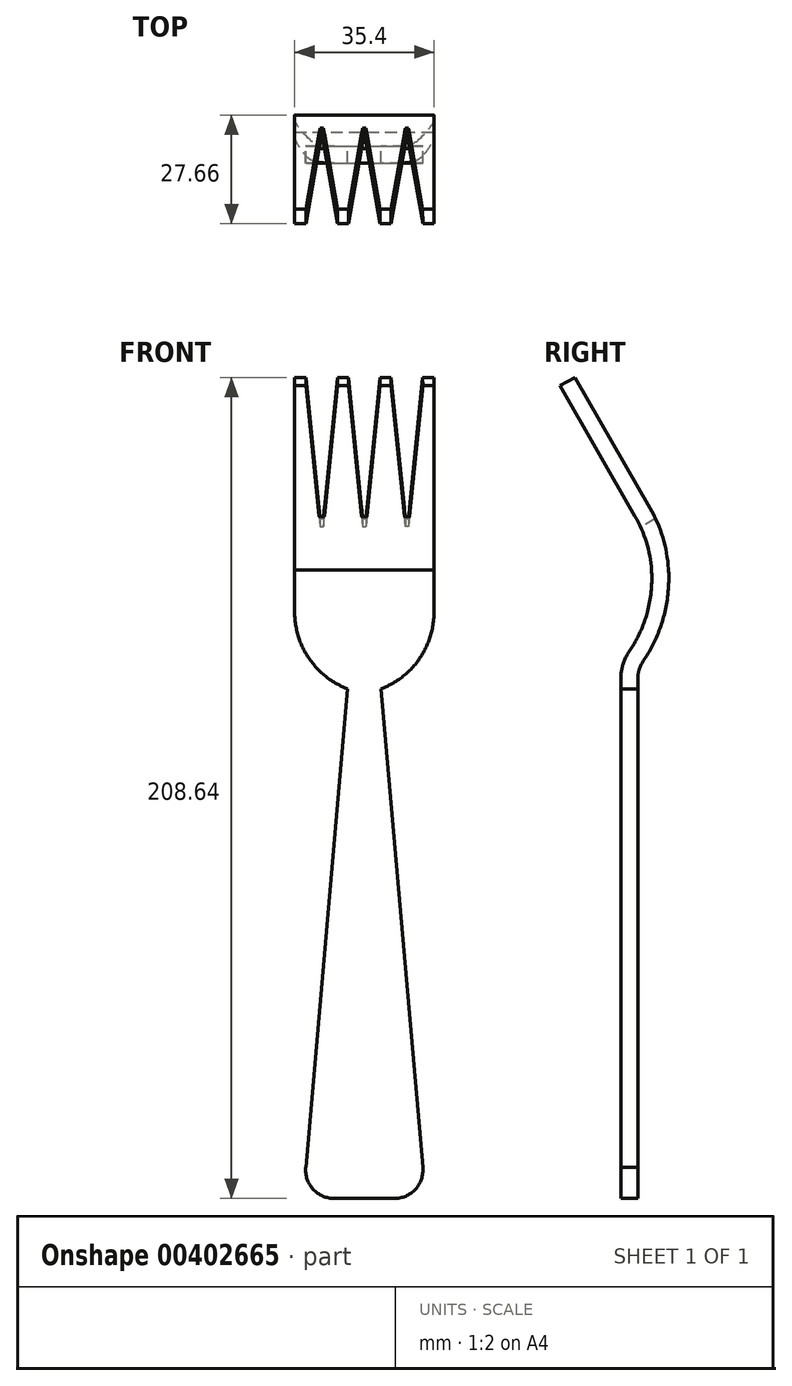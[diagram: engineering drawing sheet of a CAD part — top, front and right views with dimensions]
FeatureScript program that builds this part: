
annotation { "Feature Type Name" : "Feature", "Feature Type Description" : "" }
export const myFeature = defineFeature(function(context is Context, id is Id, definition is map)
    precondition{}
    {
        {
            var Q0;
            Q0=qCreatedBy(makeId("Front.planeOp"),FACE);
            var sketch = newSketch(context, id + "F0", { "sketchPlane" : qUnion([Q0])});
            skLineSegment(sketch, "E0", {"start": v(-7.62, -76.57) * mm, "end": v(7.62, -76.57) * mm});
            skArc(sketch, "E1", {"start": v(-7.62, -76.57) * mm, "mid": v(-12.97, -74.22) * mm, "end": v(-14.85, -68.68) * mm});
            skArc(sketch, "E2", {"start": v(7.62, -76.57) * mm, "mid": v(12.98, -74.22) * mm, "end": v(14.88, -68.68) * mm});
            skLineSegment(sketch, "E3", {"start": v(-14.85, -68.68) * mm, "end": v(14.88, -68.68) * mm});
            skLineSegment(sketch, "E4", {"start": v(-14.85, -68.68) * mm, "end": v(-7.18, 19.15) * mm});
            skLineSegment(sketch, "E5", {"start": v(-7.18, 19.15) * mm, "end": v(-4.23, 52.93) * mm});
            skLineSegment(sketch, "E6.MirrorCS", {"start": v(7.18, 19.15) * mm, "end": v(4.23, 52.93) * mm});
            skLineSegment(sketch, "E7.MirrorCS", {"start": v(14.85, -68.68) * mm, "end": v(7.18, 19.15) * mm});
            skLineSegment(sketch, "E8", {"start": v(-4.23, 52.93) * mm, "end": v(4.23, 52.93) * mm});
            skSolve(sketch);
        }
        {
            var Q0;
            Q0 = qSketchRegion(id + "F0", true);
            extrude(context, id + "F1", {"entities" : qUnion([Q0]), "depth" : 4.32 * mm});
        }
        {
            var Q0;
            Q0=qCreatedBy(makeId("Right.planeOp"),FACE);
            var sketch = newSketch(context, id + "F2", { "sketchPlane" : qUnion([Q0])});
            skPoint(sketch, "E9.0", {"position": v(-4.32, 52.93) * mm});
            skLineSegment(sketch, "E10", {"start": v(-4.32, 52.93) * mm, "end": v(-4.32, 55.36) * mm});
            skArc(sketch, "E11", {"start": v(-2.1, 62.52) * mm, "mid": v(2.37, 72.1) * mm, "end": v(3.54, 82.62) * mm});
            skPoint(sketch, "E12.visualSharp", {"position": v(-4.32, 59.64) * mm});
            skArc(sketch, "E12.filletArc", {"start": v(-2.1, 62.52) * mm, "mid": v(-3.75, 59.1) * mm, "end": v(-4.32, 55.36) * mm});
            skSolve(sketch);
        }
        {
            var Q0;
            Q0=makeQuery(id+"F1.opExtrude","SWEPT_FACE",FACE,{"disambiguationData":[OSD([sQuery(id+"F0.wireOp",EDGE,"E8")])]});
            var Q1;
            Q1=sQuery(id+"F2.wireOp",EDGE,"E10");
            var Q2;
            Q2=sQuery(id+"F2.wireOp",EDGE,"E12.filletArc");
            var Q3;
            Q3=sQuery(id+"F2.wireOp",EDGE,"E11");
            sweep(context, id + "F3", {"operationType" : NewBodyOperationType.ADD, "profiles" : qUnion([Q0]), "path" : qUnion([Q1, Q2, Q3])});
        }
        {
            var Q0;
            Q0=makeQuery(id+"F3.opSweep","CAP_FACE",FACE,{"disambiguationData":[OSD([sQuery(id+"F0.wireOp",EDGE,"E8"),sQuery(id+"F2.wireOp",VERTEX,"E11.end")])],"isStart":false});
            var sketch = newSketch(context, id + "F4", { "sketchPlane" : qUnion([Q0])});
            skLineSegment(sketch, "E13.0.0", {"start": v(4.23, 12.14) * mm, "end": v(-4.23, 12.14) * mm});
            skLineSegment(sketch, "E13.0.1", {"start": v(-4.23, 12.14) * mm, "end": v(-4.23, 7.82) * mm});
            skLineSegment(sketch, "E13.0.2", {"start": v(-4.23, 7.82) * mm, "end": v(4.23, 7.82) * mm});
            skLineSegment(sketch, "E13.0.3", {"start": v(4.23, 7.82) * mm, "end": v(4.23, 12.14) * mm});
            skSolve(sketch);
        }
        {
            var Q0;
            Q0 = qSketchRegion(id + "F4", true);
            extrude(context, id + "F5", {"entities" : qUnion([Q0]), "operationType" : NewBodyOperationType.ADD, "depth" : 0.5 * mm});
        }
        {
            var Q0;
            Q0=makeQuery(id+"F5.boolean.opBoolean","MERGE",FACE,{"derivedFrom":[makeQuery(id+"F3.opSweep","SWEPT_FACE",FACE,{"disambiguationData":[OSD([sQuery(id+"F0.wireOp",EDGE,"E6.MirrorCS"),sQuery(id+"F0.wireOp",EDGE,"E8"),sQuery(id+"F2.wireOp",EDGE,"E10")])]}),makeQuery(id+"F5.opExtrude","SWEPT_FACE",FACE,{"disambiguationData":[OSD([sQuery(id+"F4.wireOp",EDGE,"E13.0.3")])]})]});
            var sketch = newSketch(context, id + "F6", { "sketchPlane" : qUnion([Q0])});
            skLineSegment(sketch, "E14.0.0", {"start": v(0, 52.93) * mm, "end": v(0, 55.36) * mm});
            skArc(sketch, "E14.0.1", {"start": v(0, 55.36) * mm, "mid": v(0.37, 57.83) * mm, "end": v(1.46, 60.09) * mm});
            skArc(sketch, "E14.0.2", {"start": v(1.46, 60.09) * mm, "mid": v(6.52, 70.94) * mm, "end": v(7.85, 82.84) * mm});
            skLineSegment(sketch, "E14.0.3", {"start": v(7.85, 82.84) * mm, "end": v(7.82, 83.35) * mm});
            skLineSegment(sketch, "E14.0.4", {"start": v(7.82, 83.35) * mm, "end": v(3.51, 83.12) * mm});
            skLineSegment(sketch, "E14.0.5", {"start": v(3.51, 83.12) * mm, "end": v(3.54, 82.62) * mm});
            skArc(sketch, "E14.0.6", {"start": v(3.54, 82.62) * mm, "mid": v(2.37, 72.1) * mm, "end": v(-2.1, 62.52) * mm});
            skArc(sketch, "E14.0.7", {"start": v(-2.1, 62.52) * mm, "mid": v(-3.75, 59.1) * mm, "end": v(-4.32, 55.36) * mm});
            skLineSegment(sketch, "E14.0.8", {"start": v(-4.32, 55.36) * mm, "end": v(-4.32, 52.93) * mm});
            skLineSegment(sketch, "E14.0.9", {"start": v(-4.32, 52.93) * mm, "end": v(0, 52.93) * mm});
            skSolve(sketch);
        }
        {
            var Q0;
            Q0 = qSketchRegion(id + "F6", true);
            extrude(context, id + "F7", {"entities" : qUnion([Q0]), "operationType" : NewBodyOperationType.ADD, "depth" : 13.46 * mm});
        }
        {
            var Q0;
            Q0=makeQuery(id+"F1.opExtrude","SWEPT_BODY",BODY,{"disambiguationData":[OSD([sQuery(id+"F0.wireOp",EDGE,"E0"),sQuery(id+"F0.wireOp",EDGE,"E1"),sQuery(id+"F0.wireOp",EDGE,"E2"),sQuery(id+"F0.wireOp",EDGE,"E3"),sQuery(id+"F0.wireOp",EDGE,"E4"),sQuery(id+"F0.wireOp",EDGE,"E5"),sQuery(id+"F0.wireOp",EDGE,"E6.MirrorCS"),sQuery(id+"F0.wireOp",EDGE,"E7.MirrorCS"),sQuery(id+"F0.wireOp",EDGE,"E8")])]});
            var Q1;
            Q1=qCreatedBy(makeId("Right.planeOp"),FACE);
            mirror(context, id + "F8", {"operationType" : NewBodyOperationType.ADD, "entities" : qUnion([Q0]), "mirrorPlane" : qUnion([Q1])});
        }
        {
            var Q0;
            Q0=makeQuery(id+"F7.opExtrude","CAP_EDGE",EDGE,{"disambiguationData":[OSD([sQuery(id+"F6.wireOp",EDGE,"E14.0.9")])],"isStart":false});
            fillet(context, id + "F9", {"entities" : qUnion([Q0]), "radius" : 20.85 * mm, "tangentPropagation" : true, "allowEdgeOverflow" : false});
        }
        {
            var Q0;
            Q0=makeQuery(id+"F8.opPattern","COPY",EDGE,{"derivedFrom":makeQuery(id+"F7.opExtrude","CAP_EDGE",EDGE,{"disambiguationData":[OSD([sQuery(id+"F6.wireOp",EDGE,"E14.0.9")])],"isStart":false}),"instanceName":"1"});
            fillet(context, id + "F10", {"entities" : qUnion([Q0]), "radius" : 20.85 * mm, "tangentPropagation" : true, "allowEdgeOverflow" : false});
        }
        {
            var Q0;
            Q0=qCreatedBy(makeId("Right.planeOp"),FACE);
            var sketch = newSketch(context, id + "F11", { "sketchPlane" : qUnion([Q0])});
            skPoint(sketch, "E15.0", {"position": v(5.67, 83.24) * mm});
            skArc(sketch, "E16", {"start": v(5.67, 83.24) * mm, "mid": v(4.3, 90.77) * mm, "end": v(1.25, 97.8) * mm});
            skLineSegment(sketch, "E17", {"start": v(1.25, 97.8) * mm, "end": v(-17.87, 131.02) * mm});
            skSolve(sketch);
        }
        {
            var Q0;
            {var subQ0=makeQuery(id+"F7.boolean.opBoolean","MERGE",FACE,{"derivedFrom":[makeQuery(id+"F5.opExtrude","CAP_FACE",FACE,{"disambiguationData":[OSD([sQuery(id+"F4.wireOp",EDGE,"E13.0.0"),sQuery(id+"F4.wireOp",EDGE,"E13.0.1"),sQuery(id+"F4.wireOp",EDGE,"E13.0.2"),sQuery(id+"F4.wireOp",EDGE,"E13.0.3")])],"isStart":false}),makeQuery(id+"F7.opExtrude","SWEPT_FACE",FACE,{"disambiguationData":[OSD([sQuery(id+"F6.wireOp",EDGE,"E14.0.4")])]})]});Q0=makeQuery(id+"F8.boolean.opBoolean","MERGE",FACE,{"derivedFrom":[subQ0,makeQuery(id+"F8.opPattern","COPY",FACE,{"derivedFrom":subQ0,"instanceName":"1"})]});}
            var Q1;
            Q1=sQuery(id+"F11.wireOp",EDGE,"E16");
            var Q2;
            Q2=sQuery(id+"F11.wireOp",EDGE,"E17");
            sweep(context, id + "F12", {"operationType" : NewBodyOperationType.ADD, "profiles" : qUnion([Q0]), "path" : qUnion([Q1, Q2])});
        }
        {
            var Q0;
            Q0=makeQuery(id+"F12.opSweep","SWEPT_FACE",FACE,{"disambiguationData":[OSD([sQuery(id+"F4.wireOp",EDGE,"E13.0.2"),sQuery(id+"F6.wireOp",EDGE,"E14.0.4"),sQuery(id+"F6.wireOp",EDGE,"E14.0.5"),sQuery(id+"F11.wireOp",EDGE,"E17")])]});
            var sketch = newSketch(context, id + "F13", { "sketchPlane" : qUnion([Q0])});
            skLineSegment(sketch, "E18", {"start": v(0, 122.5) * mm, "end": v(0, 38.44) * mm, "construction": true});
            skPoint(sketch, "E18.endSnap0", {"position": v(0, 84.17) * mm});
            skLineSegment(sketch, "E19", {"start": v(-14.85, 122.5) * mm, "end": v(-11.23, 81.12) * mm});
            skLineSegment(sketch, "E20", {"start": v(-11.23, 81.12) * mm, "end": v(-10.42, 81.12) * mm});
            skLineSegment(sketch, "E21", {"start": v(-10.42, 81.12) * mm, "end": v(-6.8, 122.5) * mm});
            skLineSegment(sketch, "E22", {"start": v(-4.03, 122.5) * mm, "end": v(-0.4, 81.12) * mm});
            skLineSegment(sketch, "E23", {"start": v(-0.4, 81.12) * mm, "end": v(0, 81.12) * mm});
            skLineSegment(sketch, "E24.MirrorCS", {"start": v(14.85, 122.5) * mm, "end": v(11.23, 81.12) * mm});
            skLineSegment(sketch, "E25.MirrorCS", {"start": v(11.23, 81.12) * mm, "end": v(10.42, 81.12) * mm});
            skLineSegment(sketch, "E26.MirrorCS", {"start": v(10.42, 81.12) * mm, "end": v(6.8, 122.5) * mm});
            skLineSegment(sketch, "E27.MirrorCS", {"start": v(4.03, 122.5) * mm, "end": v(0.4, 81.12) * mm});
            skLineSegment(sketch, "E28.MirrorCS", {"start": v(0.4, 81.12) * mm, "end": v(0, 81.12) * mm});
            skLineSegment(sketch, "E29", {"start": v(-14.85, 122.5) * mm, "end": v(-6.8, 122.5) * mm});
            skLineSegment(sketch, "E30", {"start": v(-4.03, 122.5) * mm, "end": v(4.03, 122.5) * mm});
            skLineSegment(sketch, "E31", {"start": v(6.8, 122.5) * mm, "end": v(14.85, 122.5) * mm});
            skSolve(sketch);
        }
        {
            var Q0;
            Q0 = qSketchRegion(id + "F13", true);
            extrude(context, id + "F14", {"entities" : qUnion([Q0]), "operationType" : NewBodyOperationType.REMOVE, "oppositeDirection" : true, "depth" : 45.47 * mm});
        }
    });
